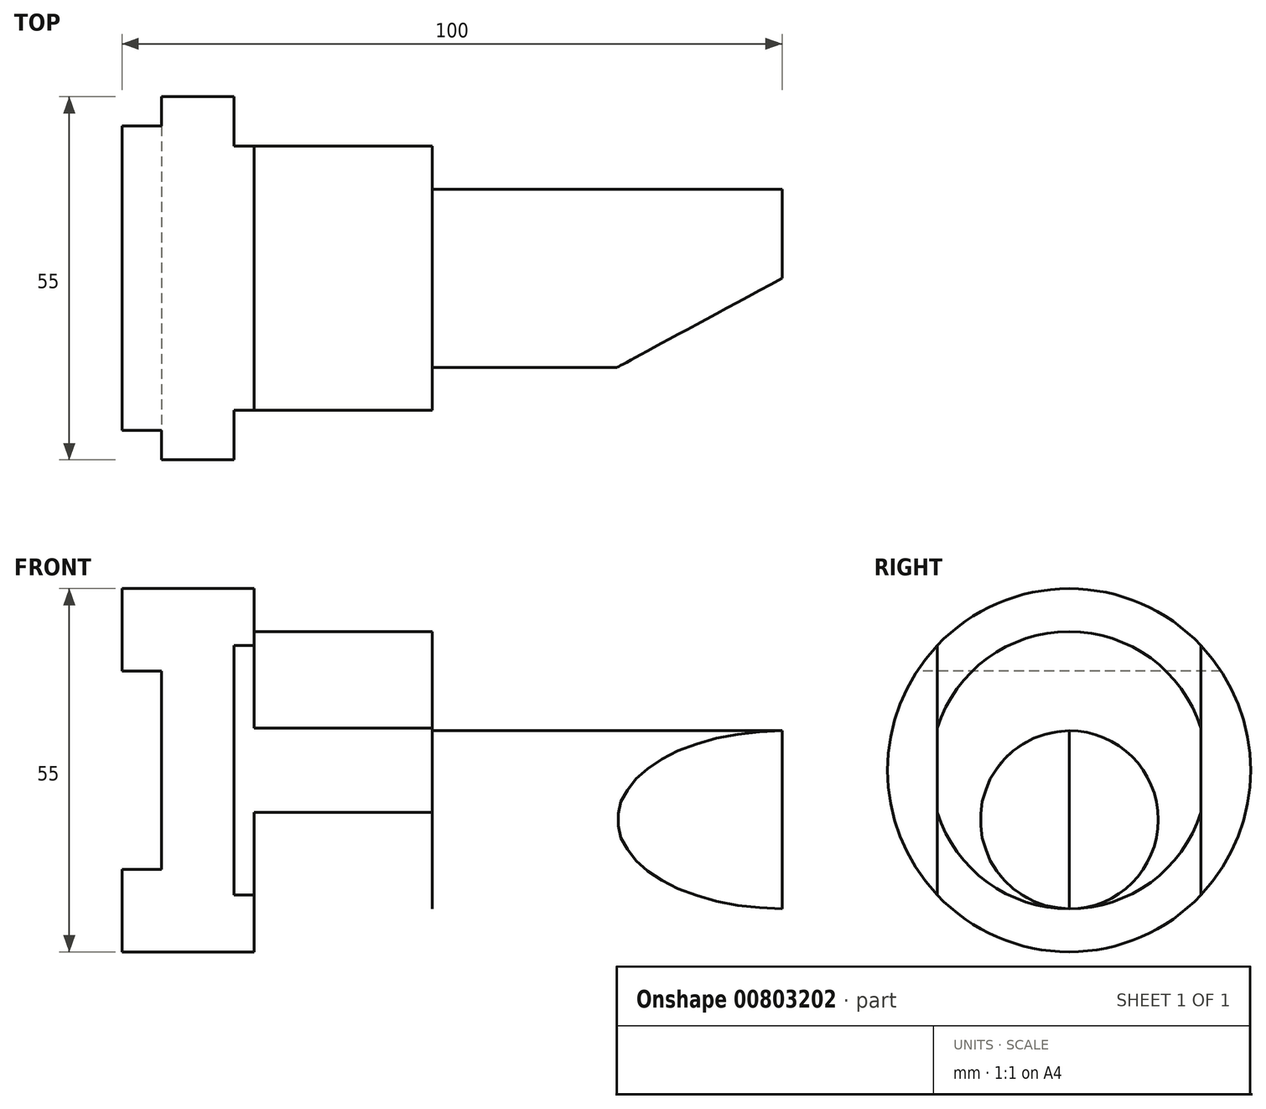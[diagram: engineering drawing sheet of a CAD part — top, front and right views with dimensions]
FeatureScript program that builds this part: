
annotation { "Feature Type Name" : "Feature", "Feature Type Description" : "" }
export const myFeature = defineFeature(function(context is Context, id is Id, definition is map)
    precondition{}
    {
        {
            var Q0;
            Q0=qCreatedBy(makeId("Front.planeOp"),FACE);
            var sketch = newSketch(context, id + "F0", { "sketchPlane" : qUnion([Q0])});
            skLineSegment(sketch, "E0", {"start": v(0, 0) * mm, "end": v(75.3, 0) * mm, "construction": true});
            skLineSegment(sketch, "E1", {"start": v(0, 0) * mm, "end": v(0, 27.5) * mm});
            skLineSegment(sketch, "E2", {"start": v(0, 27.5) * mm, "end": v(20, 27.5) * mm});
            skLineSegment(sketch, "E3", {"start": v(20, 27.5) * mm, "end": v(20, 21) * mm});
            skLineSegment(sketch, "E4", {"start": v(20, 21) * mm, "end": v(47, 21) * mm});
            skLineSegment(sketch, "E5", {"start": v(47, 21) * mm, "end": v(47, 0) * mm});
            skLineSegment(sketch, "E6", {"start": v(47, 0) * mm, "end": v(0, 0) * mm});
            skSolve(sketch);
        }
        {
            var Q0;
            Q0 = qSketchRegion(id + "F0", true);
            var Q1;
            Q1=sQuery(id+"F0.wireOp",EDGE,"E0");
            revolve(context, id + "F1", {"surfaceOperationType" : NewSurfaceOperationType.NEW, "entities" : qUnion([Q0]), "axis" : qUnion([Q1]), "revolveType" : RevolveType.FULL});
        }
        {
            var Q0;
            Q0=makeQuery(id+"F1.opRevolve","SWEPT_FACE",FACE,{"disambiguationData":[OSD([sQuery(id+"F0.wireOp",EDGE,"E5")])]});
            var sketch = newSketch(context, id + "F2", { "sketchPlane" : qUnion([Q0])});
            skCircle(sketch, "E7", {"center": v(0, -7.5) * mm, "radius": 13.5 * mm});
            skSolve(sketch);
        }
        {
            var Q0;
            Q0 = qSketchRegion(id + "F2", true);
            extrude(context, id + "F3", {"entities" : qUnion([Q0]), "operationType" : NewBodyOperationType.ADD, "depth" : (100 - 20 - 27) * mm, "offsetDistance" : 25 * mm});
        }
        {
            var Q0;
            Q0=makeQuery(id+"F1.opRevolve","SWEPT_FACE",FACE,{"disambiguationData":[OSD([sQuery(id+"F0.wireOp",EDGE,"E5")])]});
            var sketch = newSketch(context, id + "F4", { "sketchPlane" : qUnion([Q0])});
            skLineSegment(sketch, "E8", {"start": v(0, 0) * mm, "end": v(0, 17.8) * mm, "construction": true});
            skCircle(sketch, "E9.0", {"center": v(0, 0) * mm, "radius": 27.5 * mm});
            skLineSegment(sketch, "E10", {"start": v(-20, 18.87) * mm, "end": v(-20, -18.87) * mm});
            skLineSegment(sketch, "E11.MirrorCS", {"start": v(20, 18.87) * mm, "end": v(20, -18.87) * mm});
            skSolve(sketch);
        }
        {
            var Q0;
            {var subQ0=sQuery(id+"F4.wireOp",EDGE,"E10");var subQ1=makeQuery(id+"F1.opRevolve","SWEPT_EDGE",EDGE,{"disambiguationData":[OSD([sQuery(id+"F0.wireOp",EDGE,"E4"),sQuery(id+"F0.wireOp",EDGE,"E5")])]});var subQ2=makeQuery(id+"F4.imprint","INTERSECT",VERTEX,{"disambiguationData":[OD(0.0)],"derivedFrom":[subQ1,subQ0]});Q0=makeQuery(id+"F4.imprint","IMPRINT",FACE,{"disambiguationData":[TD([[makeQuery(id+"F4.imprint","IMPRINT",EDGE,{"disambiguationData":[TD([[subQ2,-1.0]])],"derivedFrom":subQ0}),-1.0]])]});}
            var Q1;
            {var subQ0=sQuery(id+"F4.wireOp",EDGE,"E10");var subQ1=sQuery(id+"F4.wireOp",EDGE,"E9.0");var subQ2=makeQuery(id+"F4.imprint","INTERSECT",VERTEX,{"disambiguationData":[OD(0.0)],"derivedFrom":[subQ1,subQ0]});Q1=makeQuery(id+"F4.imprint","IMPRINT",FACE,{"disambiguationData":[TD([[makeQuery(id+"F4.imprint","IMPRINT",EDGE,{"disambiguationData":[TD([[subQ2,-1.0]])],"derivedFrom":subQ1}),1.0]])]});}
            var Q2;
            {var subQ0=sQuery(id+"F4.wireOp",EDGE,"E11.MirrorCS");var subQ1=makeQuery(id+"F1.opRevolve","SWEPT_EDGE",EDGE,{"disambiguationData":[OSD([sQuery(id+"F0.wireOp",EDGE,"E4"),sQuery(id+"F0.wireOp",EDGE,"E5")])]});var subQ2=makeQuery(id+"F4.imprint","INTERSECT",VERTEX,{"disambiguationData":[OD(0.0)],"derivedFrom":[subQ1,subQ0]});Q2=makeQuery(id+"F4.imprint","IMPRINT",FACE,{"disambiguationData":[TD([[makeQuery(id+"F4.imprint","IMPRINT",EDGE,{"disambiguationData":[TD([[subQ2,-1.0]])],"derivedFrom":subQ0}),1.0]])]});}
            var Q3;
            {var subQ0=sQuery(id+"F4.wireOp",EDGE,"E11.MirrorCS");var subQ1=sQuery(id+"F4.wireOp",EDGE,"E9.0");var subQ2=makeQuery(id+"F4.imprint","INTERSECT",VERTEX,{"disambiguationData":[OD(0.0)],"derivedFrom":[subQ1,subQ0]});Q3=makeQuery(id+"F4.imprint","IMPRINT",FACE,{"disambiguationData":[TD([[makeQuery(id+"F4.imprint","IMPRINT",EDGE,{"disambiguationData":[TD([[subQ2,1.0]])],"derivedFrom":subQ1}),1.0]])]});}
            extrude(context, id + "F5", {"entities" : qUnion([Q0, Q1, Q2, Q3]), "operationType" : NewBodyOperationType.REMOVE, "oppositeDirection" : true, "depth" : 30 * mm, "offsetDistance" : 25 * mm});
        }
        {
            var Q0;
            Q0=qCreatedBy(makeId("Front.planeOp"),FACE);
            var sketch = newSketch(context, id + "F6", { "sketchPlane" : qUnion([Q0])});
            skLineSegment(sketch, "E12.bottom", {"start": v(0, 15) * mm, "end": v(6, 15) * mm});
            skLineSegment(sketch, "E12.top", {"start": v(0, -15) * mm, "end": v(6, -15) * mm});
            skLineSegment(sketch, "E12.left", {"start": v(0, 15) * mm, "end": v(0, -15) * mm});
            skLineSegment(sketch, "E12.right", {"start": v(6, 15) * mm, "end": v(6, -15) * mm});
            skLineSegment(sketch, "E13", {"start": v(0, 0) * mm, "end": v(14.97, 0) * mm, "construction": true});
            skSolve(sketch);
        }
        {
            var Q0;
            Q0 = qSketchRegion(id + "F6", true);
            extrude(context, id + "F7", {"entities" : qUnion([Q0]), "operationType" : NewBodyOperationType.REMOVE, "oppositeDirection" : true, "depth" : 55 * mm, "offsetDistance" : 25 * mm, "symmetric" : true});
        }
        {
            var Q0;
            Q0=qCreatedBy(makeId("Top.planeOp"),FACE);
            var sketch = newSketch(context, id + "F8", { "sketchPlane" : qUnion([Q0])});
            skLineSegment(sketch, "E14.0", {"start": v(100, 13.5) * mm, "end": v(100, -13.5) * mm});
            skLineSegment(sketch, "E15", {"start": v(100, -13.5) * mm, "end": v(47, -13.5) * mm});
            skLineSegment(sketch, "E16", {"start": v(100, 0) * mm, "end": v(75, -13.5) * mm});
            skSolve(sketch);
        }
        {
            var Q0;
            Q0 = qSketchRegion(id + "F8", true);
            extrude(context, id + "F9", {"entities" : qUnion([Q0]), "operationType" : NewBodyOperationType.REMOVE, "oppositeDirection" : true, "depth" : 50 * mm, "offsetDistance" : 25 * mm, "symmetric" : true});
        }
    });
